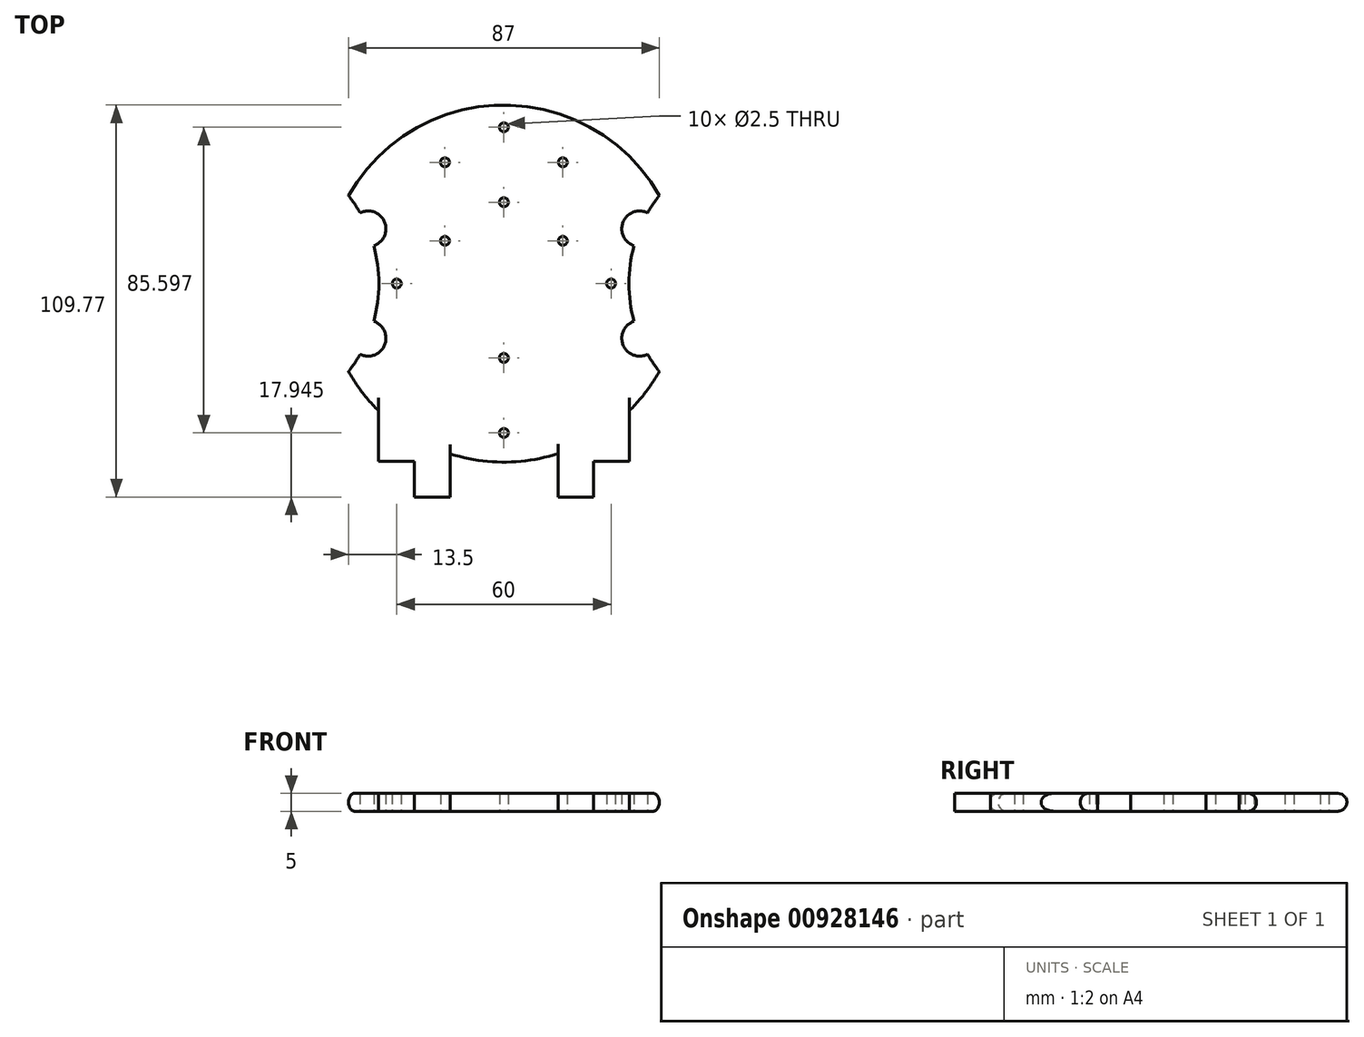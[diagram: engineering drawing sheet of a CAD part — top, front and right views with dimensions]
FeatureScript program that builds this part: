
annotation { "Feature Type Name" : "Feature", "Feature Type Description" : "" }
export const myFeature = defineFeature(function(context is Context, id is Id, definition is map)
    precondition{}
    {
        {
            var Q0;
            Q0=qCreatedBy(makeId("Top.planeOp"),FACE);
            var sketch = newSketch(context, id + "F0", { "sketchPlane" : qUnion([Q0])});
            skCircle(sketch, "E0", {"center": v(0, 0) * mm, "radius": 50 * mm});
            skSolve(sketch);
        }
        {
            var Q0;
            Q0=qCreatedBy(makeId("Top.planeOp"),FACE);
            var sketch = newSketch(context, id + "F1", { "sketchPlane" : qUnion([Q0])});
            skLineSegment(sketch, "E1.bottom", {"start": v(16.5, 11.95) * mm, "end": v(-16.5, 11.95) * mm});
            skLineSegment(sketch, "E1.top", {"start": v(16.5, 33.95) * mm, "end": v(-16.5, 33.95) * mm});
            skLineSegment(sketch, "E1.left", {"start": v(16.5, 11.95) * mm, "end": v(16.5, 33.95) * mm});
            skLineSegment(sketch, "E1.right", {"start": v(-16.5, 11.95) * mm, "end": v(-16.5, 33.95) * mm});
            skPoint(sketch, "E1.middle", {"position": v(0, 22.95) * mm});
            skSolve(sketch);
        }
        {
            var Q0;
            Q0=qCreatedBy(makeId("Top.planeOp"),FACE);
            var sketch = newSketch(context, id + "F2", { "sketchPlane" : qUnion([Q0])});
            skLineSegment(sketch, "E2.bottom", {"start": v(-30, 0) * mm, "end": v(30, 0) * mm});
            skLineSegment(sketch, "E2.top", {"start": v(-30, -12.72) * mm, "end": v(30, -12.72) * mm});
            skLineSegment(sketch, "E2.left", {"start": v(-30, 0) * mm, "end": v(-30, -12.72) * mm});
            skLineSegment(sketch, "E2.right", {"start": v(30, 0) * mm, "end": v(30, -12.72) * mm});
            skPoint(sketch, "E2.middle", {"position": v(0, -6.36) * mm});
            skSolve(sketch);
        }
        {
            var Q0;
            Q0=makeQuery(id+"F0.imprint","IMPRINT",FACE,{"disambiguationData":[TD([[makeQuery(id+"F0.imprint","IMPRINT",EDGE,{"derivedFrom":sQuery(id+"F0.wireOp",EDGE,"E0")}),1.0]])]});
            extrude(context, id + "F3", {"entities" : qUnion([Q0]), "depth" : 5 * mm, "offsetDistance" : 25 * mm});
        }
        {
            var Q0;
            Q0=makeQuery(id+"F3.opExtrude","CAP_FACE",FACE,{"disambiguationData":[OSD([sQuery(id+"F0.wireOp",EDGE,"E0")])],"isStart":false});
            fillet(context, id + "F4", {"entities" : qUnion([Q0]), "radius" : 2.5 * mm, "tangentPropagation" : true, "allowEdgeOverflow" : false});
        }
        {
            var Q0;
            Q0=makeQuery(id+"F3.opExtrude","CAP_FACE",FACE,{"disambiguationData":[OSD([sQuery(id+"F0.wireOp",EDGE,"E0")])],"isStart":true});
            fillet(context, id + "F5", {"entities" : qUnion([Q0]), "radius" : 2.5 * mm, "tangentPropagation" : true, "allowEdgeOverflow" : false});
        }
        {
            var Q0;
            Q0=sQuery(id+"F1.wireOp",VERTEX,"E1.top.end");
            var Q1;
            Q1=sQuery(id+"F1.wireOp",VERTEX,"E1.top.start");
            var Q2;
            Q2=sQuery(id+"F1.wireOp",VERTEX,"E1.bottom.start");
            var Q3;
            Q3=sQuery(id+"F1.wireOp",VERTEX,"E1.bottom.end");
            var Q4;
            Q4=sQuery(id+"F2.wireOp",VERTEX,"E2.bottom.start");
            var Q5;
            Q5=sQuery(id+"F2.wireOp",VERTEX,"E2.bottom.end");
            var Q6;
            Q6=makeQuery(id+"F3.opExtrude","SWEPT_BODY",BODY,{"disambiguationData":[OSD([sQuery(id+"F0.wireOp",EDGE,"E0")])]});
            hole(context, id + "F6", {"style" : HoleStyle.SIMPLE, "endStyle" : HoleEndStyle.THROUGH, "oppositeDirection" : true, "holeDiameter" : 2.5 * mm, "majorDiameter" : 5 * mm, "isTappedThrough" : true, "tappedDepth" : 12 * mm, "tapClearance" : 3, "locations" : qUnion([Q0, Q1, Q2, Q3, Q4, Q5]), "scope" : qUnion([Q6])});
        }
        {
            var Q0;
            Q0=qCreatedBy(makeId("Top.planeOp"),FACE);
            var sketch = newSketch(context, id + "F7", { "sketchPlane" : qUnion([Q0])});
            skLineSegment(sketch, "E3.bottom", {"start": v(0, 43.77) * mm, "end": v(19.78, 43.77) * mm});
            skLineSegment(sketch, "E3.top", {"start": v(0, 22.77) * mm, "end": v(19.78, 22.77) * mm});
            skLineSegment(sketch, "E3.left", {"start": v(0, 43.77) * mm, "end": v(0, 22.77) * mm});
            skLineSegment(sketch, "E3.right", {"start": v(19.78, 43.77) * mm, "end": v(19.78, 22.77) * mm});
            skPoint(sketch, "E3.middle", {"position": v(9.89, 33.27) * mm});
            skSolve(sketch);
        }
        {
            var Q0;
            Q0=qCreatedBy(makeId("Top.planeOp"),FACE);
            var sketch = newSketch(context, id + "F8", { "sketchPlane" : qUnion([Q0])});
            skLineSegment(sketch, "E4.bottom", {"start": v(0, -41.82) * mm, "end": v(19.78, -41.82) * mm});
            skLineSegment(sketch, "E4.top", {"start": v(0, -20.82) * mm, "end": v(19.78, -20.82) * mm});
            skLineSegment(sketch, "E4.left", {"start": v(0, -41.82) * mm, "end": v(0, -20.82) * mm});
            skLineSegment(sketch, "E4.right", {"start": v(19.78, -41.82) * mm, "end": v(19.78, -20.82) * mm});
            skPoint(sketch, "E4.middle", {"position": v(9.89, -31.32) * mm});
            skSolve(sketch);
        }
        {
            var Q0;
            Q0=sQuery(id+"F7.wireOp",VERTEX,"E3.bottom.start");
            var Q1;
            Q1=sQuery(id+"F7.wireOp",VERTEX,"E3.top.start");
            var Q2;
            Q2=sQuery(id+"F8.wireOp",VERTEX,"E4.top.start");
            var Q3;
            Q3=sQuery(id+"F8.wireOp",VERTEX,"E4.bottom.start");
            var Q4;
            Q4=makeQuery(id+"F3.opExtrude","SWEPT_BODY",BODY,{"disambiguationData":[OSD([sQuery(id+"F0.wireOp",EDGE,"E0")])]});
            hole(context, id + "F9", {"style" : HoleStyle.SIMPLE, "endStyle" : HoleEndStyle.THROUGH, "oppositeDirection" : true, "holeDiameter" : 2.5 * mm, "majorDiameter" : 5 * mm, "isTappedThrough" : true, "tappedDepth" : 12 * mm, "tapClearance" : 3, "locations" : qUnion([Q0, Q1, Q2, Q3]), "scope" : qUnion([Q4])});
        }
        {
            var Q0;
            Q0=qCreatedBy(makeId("Top.planeOp"),FACE);
            var sketch = newSketch(context, id + "F10", { "sketchPlane" : qUnion([Q0])});
            skLineSegment(sketch, "E5.bottom", {"start": v(-75, 0) * mm, "end": v(75, 0) * mm});
            skLineSegment(sketch, "E5.top", {"start": v(-75, -25) * mm, "end": v(75, -25) * mm});
            skLineSegment(sketch, "E5.left", {"start": v(-75, 0) * mm, "end": v(-75, -25) * mm});
            skLineSegment(sketch, "E5.right", {"start": v(75, 0) * mm, "end": v(75, -25) * mm});
            skPoint(sketch, "E5.middle", {"position": v(0, -12.5) * mm});
            skSolve(sketch);
        }
        {
            var Q0;
            Q0=sQuery(id+"F10.wireOp",VERTEX,"E5.bottom.start");
            var Q1;
            Q1=sQuery(id+"F10.wireOp",VERTEX,"E5.bottom.end");
            var Q2;
            Q2=makeQuery(id+"F3.opExtrude","SWEPT_BODY",BODY,{"disambiguationData":[OSD([sQuery(id+"F0.wireOp",EDGE,"E0")])]});
            hole(context, id + "F11", {"style" : HoleStyle.SIMPLE, "endStyle" : HoleEndStyle.THROUGH, "oppositeDirection" : true, "holeDiameter" : 80 * mm, "majorDiameter" : 5 * mm, "isTappedThrough" : true, "tappedDepth" : 12 * mm, "tapClearance" : 3, "locations" : qUnion([Q0, Q1]), "scope" : qUnion([Q2])});
        }
        {
            var Q0;
            Q0=qCreatedBy(makeId("Top.planeOp"),FACE);
            var sketch = newSketch(context, id + "F12", { "sketchPlane" : qUnion([Q0])});
            skLineSegment(sketch, "E6.bottom", {"start": v(38.01, 15.33) * mm, "end": v(-38.01, 15.33) * mm});
            skLineSegment(sketch, "E6.top", {"start": v(38.01, -15.33) * mm, "end": v(-38.01, -15.33) * mm});
            skLineSegment(sketch, "E6.left", {"start": v(38.01, 15.33) * mm, "end": v(38.01, -15.33) * mm});
            skLineSegment(sketch, "E6.right", {"start": v(-38.01, 15.33) * mm, "end": v(-38.01, -15.33) * mm});
            skPoint(sketch, "E6.middle", {"position": v(0, 0) * mm});
            skSolve(sketch);
        }
        {
            var Q0;
            Q0=sQuery(id+"F12.wireOp",VERTEX,"E6.bottom.end");
            var Q1;
            Q1=sQuery(id+"F12.wireOp",VERTEX,"E6.top.end");
            var Q2;
            Q2=sQuery(id+"F12.wireOp",VERTEX,"E6.bottom.start");
            var Q3;
            Q3=sQuery(id+"F12.wireOp",VERTEX,"E6.top.start");
            var Q4;
            Q4=makeQuery(id+"F3.opExtrude","SWEPT_BODY",BODY,{"disambiguationData":[OSD([sQuery(id+"F0.wireOp",EDGE,"E0")])]});
            hole(context, id + "F13", {"style" : HoleStyle.SIMPLE, "endStyle" : HoleEndStyle.THROUGH, "oppositeDirection" : true, "holeDiameter" : 10 * mm, "majorDiameter" : 5 * mm, "isTappedThrough" : true, "tappedDepth" : 12 * mm, "tapClearance" : 3, "locations" : qUnion([Q0, Q1, Q2, Q3]), "scope" : qUnion([Q4])});
        }
        {
            var Q0;
            Q0=makeQuery(id+"F3.opExtrude","CAP_FACE",FACE,{"disambiguationData":[OSD([sQuery(id+"F0.wireOp",EDGE,"E0")])],"isStart":false});
            var sketch = newSketch(context, id + "F14", { "sketchPlane" : qUnion([Q0])});
            skLineSegment(sketch, "E7.bottom", {"start": v(-14.97, -24.77) * mm, "end": v(-35.11, -24.77) * mm});
            skLineSegment(sketch, "E7.top", {"start": v(-14.97, -55.07) * mm, "end": v(-35.11, -55.07) * mm});
            skLineSegment(sketch, "E7.left", {"start": v(-14.97, -24.77) * mm, "end": v(-14.97, -55.07) * mm});
            skLineSegment(sketch, "E7.right", {"start": v(-35.11, -24.77) * mm, "end": v(-35.11, -55.07) * mm});
            skSolve(sketch);
        }
        {
            var Q0;
            {var subQ29=sQuery(id+"F14.wireOp",EDGE,"E7.bottom");Q0=makeQuery(id+"F14.imprint","IMPRINT",FACE,{"disambiguationData":[TD([[makeQuery(id+"F14.imprint","IMPRINT",EDGE,{"derivedFrom":subQ29}),-1.0]])]});}
            var sketch = newSketch(context, id + "F15", { "sketchPlane" : qUnion([Q0])});
            skLineSegment(sketch, "E8.bottom", {"start": v(35.11, -54.89) * mm, "end": v(15.15, -54.89) * mm});
            skLineSegment(sketch, "E8.top", {"start": v(35.11, -24.77) * mm, "end": v(15.15, -24.77) * mm});
            skLineSegment(sketch, "E8.left", {"start": v(35.11, -54.89) * mm, "end": v(35.11, -24.77) * mm});
            skLineSegment(sketch, "E8.right", {"start": v(15.15, -54.89) * mm, "end": v(15.15, -24.77) * mm});
            skSolve(sketch);
        }
        {
            var Q0;
            {var subQ0=sQuery(id+"F15.wireOp",EDGE,"E8.top");Q0=makeQuery(id+"F15.imprint","IMPRINT",FACE,{"disambiguationData":[TD([[makeQuery(id+"F15.imprint","IMPRINT",EDGE,{"derivedFrom":subQ0}),1.0]])]});}
            var Q1;
            {var subQ0=sQuery(id+"F14.wireOp",EDGE,"E7.bottom");Q1=makeQuery(id+"F14.imprint","IMPRINT",FACE,{"disambiguationData":[TD([[makeQuery(id+"F14.imprint","IMPRINT",EDGE,{"derivedFrom":subQ0}),1.0]])]});}
            extrude(context, id + "F16", {"entities" : qUnion([Q0, Q1]), "operationType" : NewBodyOperationType.REMOVE, "oppositeDirection" : true, "depth" : 5 * mm, "offsetDistance" : 25 * mm});
        }
        {
            var Q0;
            Q0=makeQuery(id+"F16.boolean.opBoolean","COPY",FACE,{"derivedFrom":makeQuery(id+"F16.opExtrude","SWEPT_FACE",FACE,{"disambiguationData":[OSD([sQuery(id+"F14.wireOp",EDGE,"E7.bottom")])]})});
            extrude(context, id + "F17", {"entities" : qUnion([Q0]), "operationType" : NewBodyOperationType.ADD, "depth" : 25 * mm, "offsetDistance" : 25 * mm});
        }
        {
            var Q0;
            Q0=makeQuery(id+"F16.boolean.opBoolean","COPY",FACE,{"derivedFrom":makeQuery(id+"F16.opExtrude","SWEPT_FACE",FACE,{"disambiguationData":[OSD([sQuery(id+"F15.wireOp",EDGE,"E8.top")])]})});
            extrude(context, id + "F18", {"entities" : qUnion([Q0]), "operationType" : NewBodyOperationType.ADD, "depth" : 25 * mm, "offsetDistance" : 25 * mm});
        }
        {
            var Q0;
            Q0=makeQuery(id+"F17.opExtrude","CAP_FACE",FACE,{"disambiguationData":[OSD([sQuery(id+"F14.wireOp",EDGE,"E7.bottom")])],"isStart":false});
            var sketch = newSketch(context, id + "F19", { "sketchPlane" : qUnion([Q0])});
            skLineSegment(sketch, "E9.bottom", {"start": v(-14.97, 5) * mm, "end": v(-25.04, 5) * mm});
            skLineSegment(sketch, "E9.top", {"start": v(-14.97, 0) * mm, "end": v(-25.04, 0) * mm});
            skLineSegment(sketch, "E9.left", {"start": v(-14.97, 5) * mm, "end": v(-14.97, 0) * mm});
            skLineSegment(sketch, "E9.right", {"start": v(-25.04, 5) * mm, "end": v(-25.04, 0) * mm});
            skSolve(sketch);
        }
        {
            var Q0;
            Q0=makeQuery(id+"F18.opExtrude","CAP_FACE",FACE,{"disambiguationData":[OSD([sQuery(id+"F15.wireOp",EDGE,"E8.top")])],"isStart":false});
            var sketch = newSketch(context, id + "F20", { "sketchPlane" : qUnion([Q0])});
            skLineSegment(sketch, "E10.bottom", {"start": v(15.15, 5) * mm, "end": v(25.13, 5) * mm});
            skLineSegment(sketch, "E10.top", {"start": v(15.15, 0) * mm, "end": v(25.13, 0) * mm});
            skLineSegment(sketch, "E10.left", {"start": v(15.15, 5) * mm, "end": v(15.15, 0) * mm});
            skLineSegment(sketch, "E10.right", {"start": v(25.13, 5) * mm, "end": v(25.13, 0) * mm});
            skSolve(sketch);
        }
        {
            var Q0;
            Q0=makeQuery(id+"F19.imprint","IMPRINT",FACE,{"disambiguationData":[TD([[makeQuery(id+"F19.imprint","IMPRINT",EDGE,{"derivedFrom":sQuery(id+"F19.wireOp",EDGE,"E9.bottom")}),1.0]])]});
            extrude(context, id + "F21", {"entities" : qUnion([Q0]), "operationType" : NewBodyOperationType.ADD, "depth" : 10 * mm, "offsetDistance" : 25 * mm});
        }
        {
            var Q0;
            Q0=makeQuery(id+"F20.imprint","IMPRINT",FACE,{"disambiguationData":[TD([[makeQuery(id+"F20.imprint","IMPRINT",EDGE,{"derivedFrom":sQuery(id+"F20.wireOp",EDGE,"E10.bottom")}),1.0]])]});
            extrude(context, id + "F22", {"entities" : qUnion([Q0]), "operationType" : NewBodyOperationType.ADD, "depth" : 10 * mm, "offsetDistance" : 25 * mm});
        }
    });
